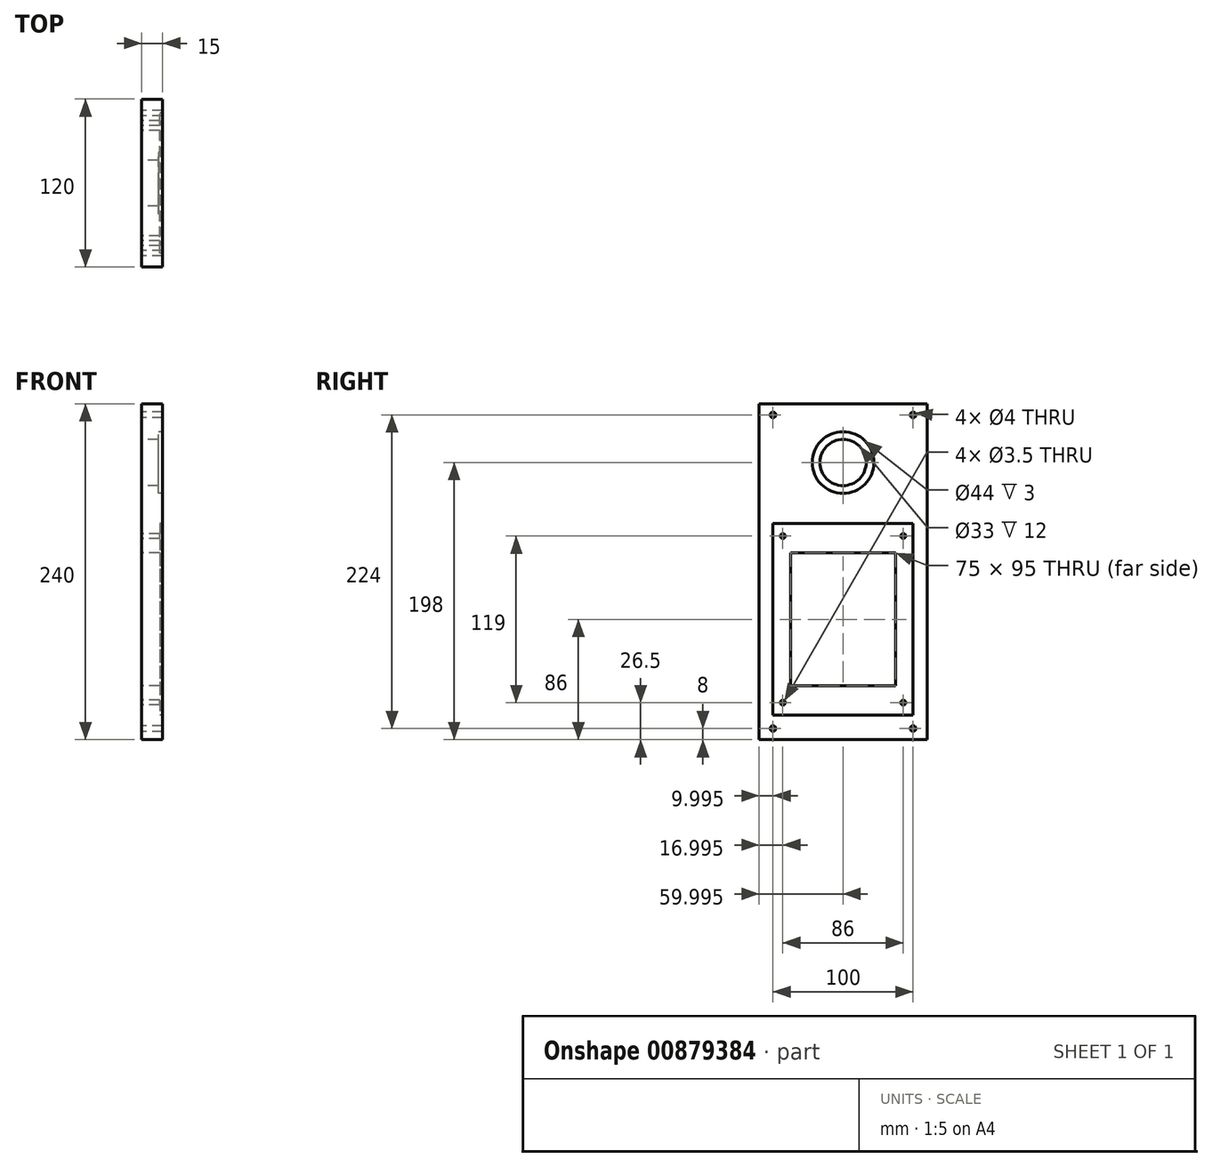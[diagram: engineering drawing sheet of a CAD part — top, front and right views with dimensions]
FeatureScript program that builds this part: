
annotation { "Feature Type Name" : "Feature", "Feature Type Description" : "" }
export const myFeature = defineFeature(function(context is Context, id is Id, definition is map)
    precondition{}
    {
        {
            var Q0;
            Q0=qCreatedBy(makeId("Right.planeOp"),FACE);
            var sketch = newSketch(context, id + "F0", { "sketchPlane" : qUnion([Q0])});
            skLineSegment(sketch, "E0.bottom", {"start": v(-70.43, 120) * mm, "end": v(49.57, 120) * mm});
            skLineSegment(sketch, "E0.top", {"start": v(-70.43, -120) * mm, "end": v(49.57, -120) * mm});
            skLineSegment(sketch, "E0.left", {"start": v(-70.43, 120) * mm, "end": v(-70.43, -120) * mm});
            skPoint(sketch, "E0.middle", {"position": v(0, 0) * mm});
            skLineSegment(sketch, "E1.left", {"start": v(-60.43, 25.45) * mm, "end": v(-60.43, -102.5) * mm});
            skLineSegment(sketch, "E1.right", {"start": v(39.57, 25.45) * mm, "end": v(39.57, -102.5) * mm});
            skPoint(sketch, "E2", {"position": v(-10.43, -102.5) * mm});
            skPoint(sketch, "E3", {"position": v(-10.43, -34) * mm});
            skLineSegment(sketch, "E4.bottom", {"start": v(-60.43, 34.5) * mm, "end": v(39.57, 34.5) * mm});
            skLineSegment(sketch, "E4.left", {"start": v(-60.43, 34.5) * mm, "end": v(-60.43, -102.5) * mm});
            skLineSegment(sketch, "E4.right", {"start": v(39.57, 34.5) * mm, "end": v(39.57, -102.5) * mm});
            skLineSegment(sketch, "E5", {"start": v(-60.43, -102.5) * mm, "end": v(39.57, -102.5) * mm});
            skLineSegment(sketch, "E6.bottom", {"start": v(27.07, 13.5) * mm, "end": v(-47.93, 13.5) * mm});
            skLineSegment(sketch, "E6.top", {"start": v(27.07, -81.5) * mm, "end": v(-47.93, -81.5) * mm});
            skLineSegment(sketch, "E6.left", {"start": v(27.07, 13.5) * mm, "end": v(27.07, -81.5) * mm});
            skLineSegment(sketch, "E6.right", {"start": v(-47.93, 13.5) * mm, "end": v(-47.93, -81.5) * mm});
            skCircle(sketch, "E7", {"center": v(-10.43, 78) * mm, "radius": 22 * mm});
            skCircle(sketch, "E8", {"center": v(-10.43, 78) * mm, "radius": 16.5 * mm});
            skLineSegment(sketch, "E9", {"start": v(49.57, 120) * mm, "end": v(49.57, -120) * mm});
            skPoint(sketch, "E0.right.start.orphan", {"position": v(70.43, 120) * mm});
            skPoint(sketch, "E10.orphan", {"position": v(-10.43, 120) * mm});
            skPoint(sketch, "E11.trimOffspring.end.orphan", {"position": v(-10.43, -120) * mm});
            skPoint(sketch, "E12", {"position": v(-53.43, 25.5) * mm});
            skPoint(sketch, "E13", {"position": v(32.57, 25.5) * mm});
            skCircle(sketch, "E14", {"center": v(-53.43, 25.5) * mm, "radius": 1.75 * mm});
            skCircle(sketch, "E15", {"center": v(32.57, 25.5) * mm, "radius": 1.75 * mm});
            skCircle(sketch, "E16.0.1.0", {"center": v(-53.43, -93.5) * mm, "radius": 1.75 * mm});
            skCircle(sketch, "E17.0.1.0", {"center": v(32.57, -93.5) * mm, "radius": 1.75 * mm});
            skLineSegment(sketch, "E17.direction1", {"start": v(32.57, 25.5) * mm, "end": v(34.32, 25.5) * mm, "construction": true});
            skCircle(sketch, "E18.0.1.0", {"center": v(-60.43, 112) * mm, "radius": 2 * mm});
            skCircle(sketch, "E19.0.1.0", {"center": v(39.57, 112) * mm, "radius": 2 * mm});
            skCircle(sketch, "E20.0.1.0", {"center": v(39.57, -112) * mm, "radius": 2 * mm});
            skCircle(sketch, "E21.0.1.0", {"center": v(-60.43, -112) * mm, "radius": 2 * mm});
            skSolve(sketch);
        }
        {
            var Q0;
            {var subQ12=sQuery(id+"F0.wireOp",EDGE,"E0.left");Q0=makeQuery(id+"F0.imprint","IMPRINT",FACE,{"disambiguationData":[TD([[makeQuery(id+"F0.imprint","IMPRINT",EDGE,{"derivedFrom":subQ12}),1.0]])]});}
            var Q1;
            {var subQ11=sQuery(id+"F0.wireOp",EDGE,"E0.right");Q1=makeQuery(id+"F0.imprint","IMPRINT",FACE,{"disambiguationData":[TD([[makeQuery(id+"F0.imprint","IMPRINT",EDGE,{"derivedFrom":subQ11}),-1.0]])]});}
            extrude(context, id + "F1", {"entities" : qUnion([Q0, Q1]), "depth" : 15 * mm, "offsetDistance" : 25 * mm});
        }
        {
            var Q0;
            Q0=makeQuery(id+"F0.imprint","IMPRINT",FACE,{"disambiguationData":[TD([[makeQuery(id+"F0.imprint","IMPRINT",EDGE,{"derivedFrom":sQuery(id+"F0.wireOp",EDGE,"E7")}),1.0]])]});
            extrude(context, id + "F2", {"entities" : qUnion([Q0]), "operationType" : NewBodyOperationType.ADD, "depth" : 12 * mm, "offsetDistance" : 25 * mm});
        }
        {
            var Q0;
            {var subQ1=sQuery(id+"F0.wireOp",EDGE,"E4.bottom");Q0=makeQuery(id+"F0.imprint","IMPRINT",FACE,{"disambiguationData":[TD([[makeQuery(id+"F0.imprint","IMPRINT",EDGE,{"derivedFrom":subQ1}),-1.0]])]});}
            extrude(context, id + "F3", {"entities" : qUnion([Q0]), "operationType" : NewBodyOperationType.ADD, "depth" : 13 * mm, "offsetDistance" : 25 * mm});
        }
    });
